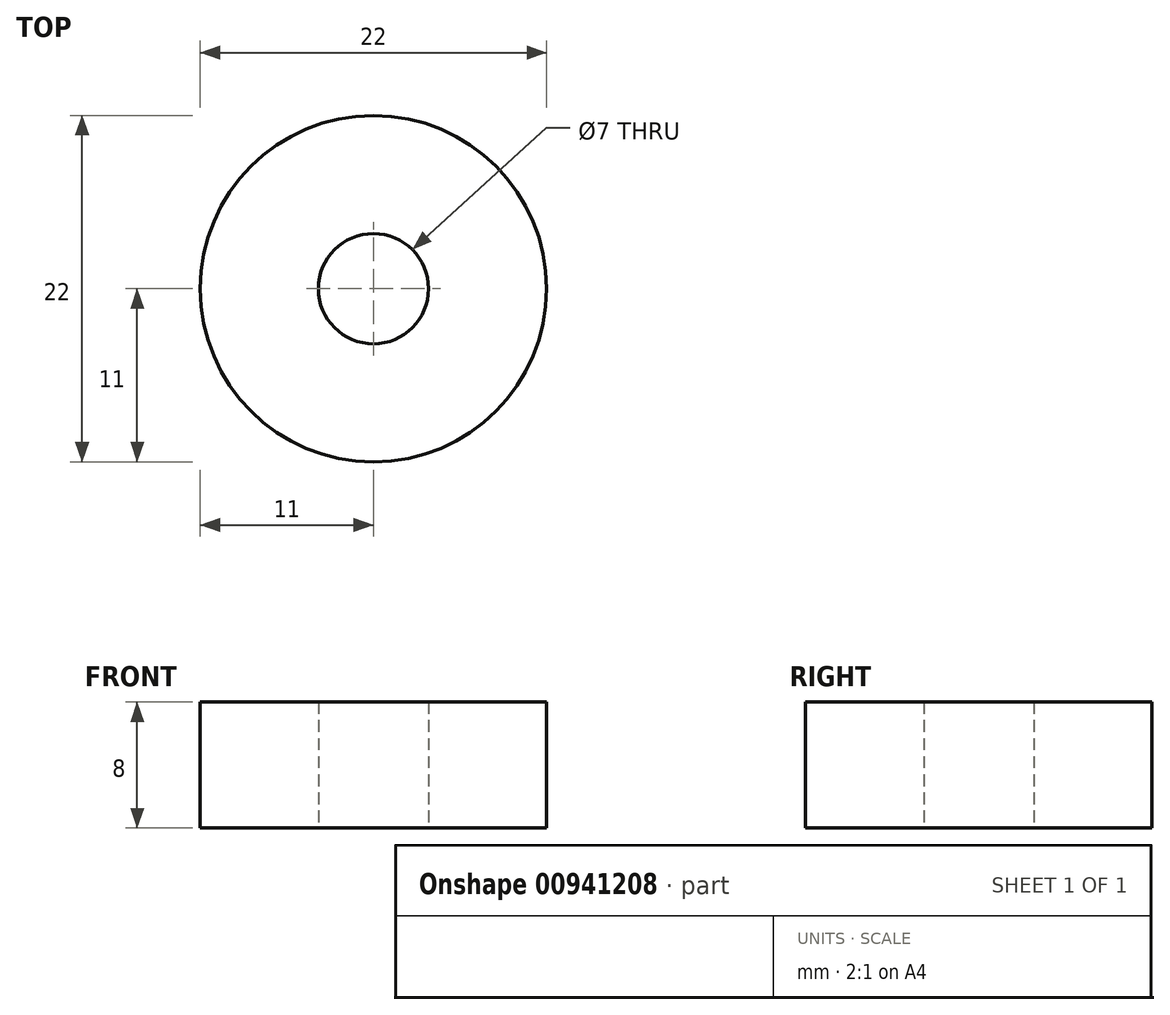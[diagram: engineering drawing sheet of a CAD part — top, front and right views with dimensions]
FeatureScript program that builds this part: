
annotation { "Feature Type Name" : "Feature", "Feature Type Description" : "" }
export const myFeature = defineFeature(function(context is Context, id is Id, definition is map)
    precondition{}
    {
        {
            var Q0;
            Q0=qCreatedBy(makeId("Top.planeOp"),FACE);
            var sketch = newSketch(context, id + "F0", { "sketchPlane" : qUnion([Q0])});
            skCircle(sketch, "E0", {"center": v(0, 0) * mm, "radius": 3.5 * mm});
            skCircle(sketch, "E1", {"center": v(0, 0) * mm, "radius": 11 * mm});
            skSolve(sketch);
        }
        {
            var Q0;
            Q0=makeQuery(id+"F0.imprint","IMPRINT",FACE,{"disambiguationData":[TD([[makeQuery(id+"F0.imprint","IMPRINT",EDGE,{"derivedFrom":sQuery(id+"F0.wireOp",EDGE,"E0")}),-1.0]])]});
            extrude(context, id + "F1", {"entities" : qUnion([Q0]), "depth" : 8 * mm, "offsetDistance" : 25 * mm});
        }
    });
